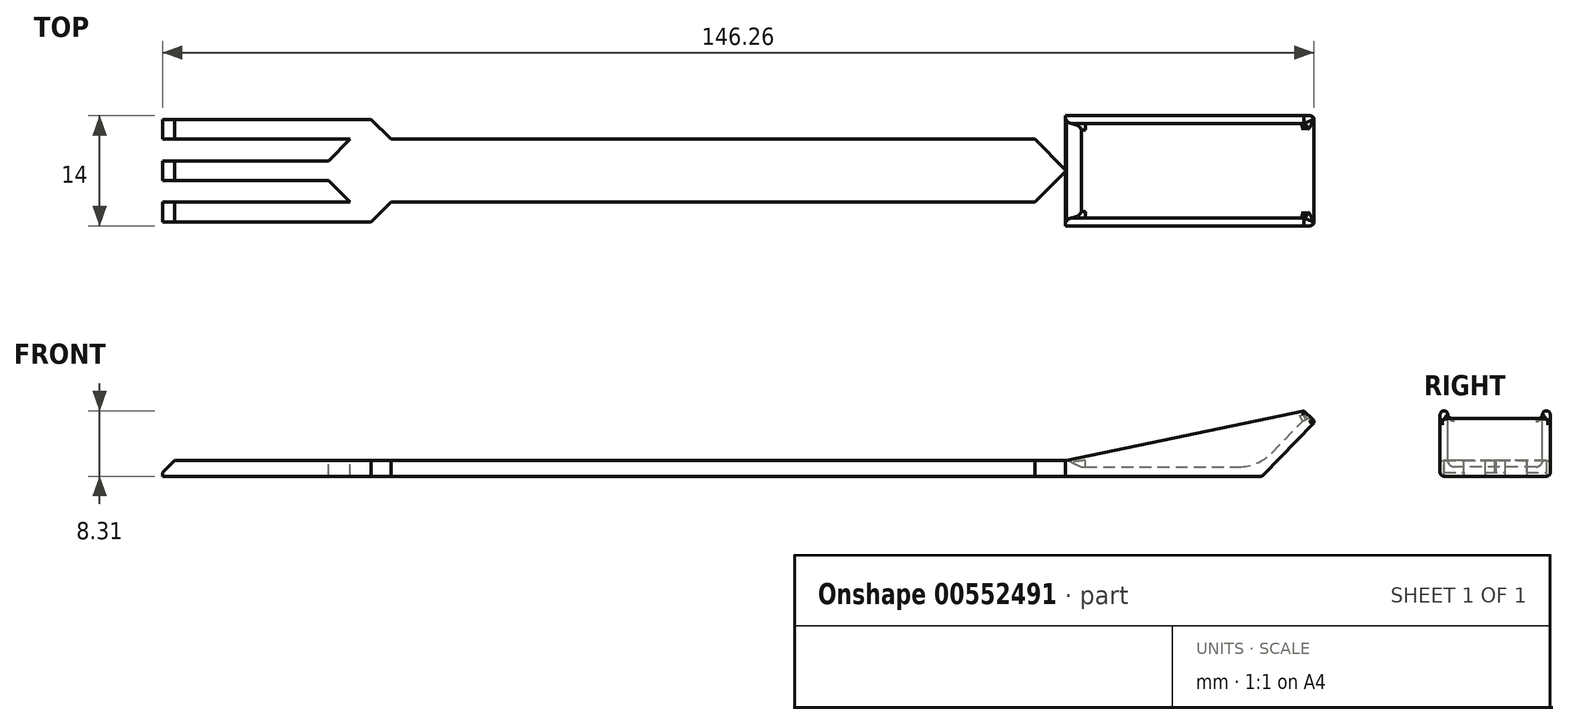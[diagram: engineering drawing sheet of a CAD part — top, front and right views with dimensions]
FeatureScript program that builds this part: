
annotation { "Feature Type Name" : "Feature", "Feature Type Description" : "" }
export const myFeature = defineFeature(function(context is Context, id is Id, definition is map)
    precondition{}
    {
        {
            var Q0;
            Q0=qCreatedBy(makeId("Top.planeOp"),FACE);
            var sketch = newSketch(context, id + "F0", { "sketchPlane" : qUnion([Q0])});
            skLineSegment(sketch, "E0.bottom", {"start": v(-44.04, 8) * mm, "end": v(45.74, 8) * mm});
            skLineSegment(sketch, "E0.top", {"start": v(-44.04, 0) * mm, "end": v(45.74, 0) * mm});
            skLineSegment(sketch, "E1.bottom", {"start": v(-44.5, 8) * mm, "end": v(-69.04, 8) * mm});
            skLineSegment(sketch, "E1.top", {"start": v(-44.04, 10.5) * mm, "end": v(-69.04, 10.5) * mm});
            skLineSegment(sketch, "E1.left", {"start": v(-44.04, 8) * mm, "end": v(-44.04, 10.5) * mm});
            skLineSegment(sketch, "E1.right", {"start": v(-69.04, 8) * mm, "end": v(-69.04, 10.5) * mm});
            skLineSegment(sketch, "E2.bottom", {"start": v(-44.5, 0) * mm, "end": v(-69.04, 0) * mm});
            skLineSegment(sketch, "E2.top", {"start": v(-44.04, -2.5) * mm, "end": v(-69.04, -2.5) * mm});
            skLineSegment(sketch, "E2.left", {"start": v(-44.04, 0) * mm, "end": v(-44.04, -2.5) * mm});
            skLineSegment(sketch, "E2.right", {"start": v(-69.04, 0) * mm, "end": v(-69.04, -2.5) * mm});
            skPoint(sketch, "E3.left.start.orphan", {"position": v(-44.04, 4) * mm});
            skPoint(sketch, "E3.right.end.orphan", {"position": v(-69.04, 2.75) * mm});
            skLineSegment(sketch, "E4.bottom", {"start": v(-69.04, 2.75) * mm, "end": v(-44.5, 2.75) * mm});
            skLineSegment(sketch, "E4.top", {"start": v(-69.04, 5.25) * mm, "end": v(-44.5, 5.25) * mm});
            skLineSegment(sketch, "E4.left", {"start": v(-69.04, 2.75) * mm, "end": v(-69.04, 5.25) * mm});
            skLineSegment(sketch, "E5.bottom", {"start": v(-44.04, 10.5) * mm, "end": v(-44.5, 10.5) * mm});
            skLineSegment(sketch, "E5.top", {"start": v(-44.04, -2.5) * mm, "end": v(-44.5, -2.5) * mm});
            skLineSegment(sketch, "E5.left", {"start": v(-44.04, 10.5) * mm, "end": v(-44.04, 8) * mm});
            skLineSegment(sketch, "E5.right", {"start": v(-44.5, 8) * mm, "end": v(-44.5, 5.25) * mm});
            skLineSegment(sketch, "E6.trimOffspring", {"start": v(-44.5, 2.75) * mm, "end": v(-44.5, 0) * mm});
            skLineSegment(sketch, "E7", {"start": v(45.74, 8) * mm, "end": v(45.74, 0) * mm});
            skSolve(sketch);
        }
        {
            var Q0;
            Q0 = qSketchRegion(id + "F0", true);
            extrude(context, id + "F1", {"entities" : qUnion([Q0]), "depth" : 2 * mm, "offsetDistance" : 25 * mm});
        }
        {
            var Q0;
            Q0=makeQuery(id+"F1.opExtrude","SWEPT_EDGE",EDGE,{"disambiguationData":[OSD([sQuery(id+"F0.wireOp",EDGE,"E0.top"),sQuery(id+"F0.wireOp",EDGE,"E2.left")])]});
            var Q1;
            Q1=makeQuery(id+"F1.opExtrude","SWEPT_EDGE",EDGE,{"disambiguationData":[OSD([sQuery(id+"F0.wireOp",EDGE,"E0.bottom"),sQuery(id+"F0.wireOp",EDGE,"E5.left")])]});
            chamfer(context, id + "F2", {"entities" : qUnion([Q0, Q1]), "width" : 4 * mm, "tangentPropagation" : true});
        }
        {
            var Q0;
            Q0=makeQuery(id+"F1.opExtrude","SWEPT_EDGE",EDGE,{"disambiguationData":[OSD([sQuery(id+"F0.wireOp",EDGE,"E4.bottom"),sQuery(id+"F0.wireOp",EDGE,"E6.trimOffspring")])]});
            var Q1;
            Q1=makeQuery(id+"F1.opExtrude","SWEPT_EDGE",EDGE,{"disambiguationData":[OSD([sQuery(id+"F0.wireOp",EDGE,"E4.top"),sQuery(id+"F0.wireOp",EDGE,"E5.right")])]});
            chamfer(context, id + "F3", {"entities" : qUnion([Q0, Q1]), "width" : 3.5 * mm, "tangentPropagation" : true});
        }
        {
            var Q0;
            Q0=qCreatedBy(makeId("Front.planeOp"),FACE);
            var sketch = newSketch(context, id + "F4", { "sketchPlane" : qUnion([Q0])});
            skLineSegment(sketch, "E8", {"start": v(45.64, 0) * mm, "end": v(70.64, 0) * mm});
            skLineSegment(sketch, "E9", {"start": v(70.64, 0) * mm, "end": v(77.36, 6.93) * mm});
            skLineSegment(sketch, "E10", {"start": v(77.36, 6.93) * mm, "end": v(75.93, 8.31) * mm});
            skLineSegment(sketch, "E11", {"start": v(75.93, 8.31) * mm, "end": v(45.64, 2) * mm});
            skLineSegment(sketch, "E12", {"start": v(45.64, 2) * mm, "end": v(45.64, 0) * mm});
            skSolve(sketch);
        }
        {
            var Q0;
            Q0=makeQuery(id+"F4.imprint","IMPRINT",FACE,{"disambiguationData":[TD([[makeQuery(id+"F4.imprint","IMPRINT",EDGE,{"derivedFrom":sQuery(id+"F4.wireOp",EDGE,"E8")}),1.0]])]});
            extrude(context, id + "F5", {"entities" : qUnion([Q0]), "operationType" : NewBodyOperationType.ADD, "oppositeDirection" : true, "depth" : 11 * mm, "offsetDistance" : 25 * mm});
        }
        {
            var Q0;
            Q0 = qSketchRegion(id + "F4", true);
            extrude(context, id + "F6", {"entities" : qUnion([Q0]), "operationType" : NewBodyOperationType.ADD, "depth" : 3 * mm, "offsetDistance" : 25 * mm});
        }
        {
            var Q0;
            Q0=qCreatedBy(makeId("Front.planeOp"),FACE);
            var sketch = newSketch(context, id + "F7", { "sketchPlane" : qUnion([Q0])});
            skLineSegment(sketch, "E13.0", {"start": v(40.64, 2) * mm, "end": v(40.64, 0) * mm});
            skLineSegment(sketch, "E14.2", {"start": v(70.13, 1.2) * mm, "end": v(75.66, 6.9) * mm});
            skLineSegment(sketch, "E14.3", {"start": v(47.64, 1.2) * mm, "end": v(70.13, 1.2) * mm});
            skLineSegment(sketch, "E15", {"start": v(47.64, 1.2) * mm, "end": v(45.28, 2.26) * mm});
            skLineSegment(sketch, "E16", {"start": v(45.28, 2.26) * mm, "end": v(75.32, 10.8) * mm});
            skLineSegment(sketch, "E17", {"start": v(75.32, 10.8) * mm, "end": v(80.5, 9.3) * mm});
            skLineSegment(sketch, "E18", {"start": v(80.5, 9.3) * mm, "end": v(75.66, 6.9) * mm});
            skSolve(sketch);
        }
        {
            var Q0;
            Q0=makeQuery(id+"F7.imprint","IMPRINT",FACE,{"disambiguationData":[TD([[makeQuery(id+"F7.imprint","IMPRINT",EDGE,{"derivedFrom":sQuery(id+"F7.wireOp",EDGE,"E14.2")}),1.0]])]});
            extrude(context, id + "F8", {"entities" : qUnion([Q0]), "operationType" : NewBodyOperationType.REMOVE, "oppositeDirection" : true, "depth" : 10 * mm, "offsetDistance" : 25 * mm});
        }
        {
            var Q0;
            Q0 = qSketchRegion(id + "F7", true);
            extrude(context, id + "F9", {"entities" : qUnion([Q0]), "operationType" : NewBodyOperationType.REMOVE, "oppositeDirection" : true, "depth" : -2 * mm, "offsetDistance" : 25 * mm});
        }
        {
            var Q0;
            {var subQ0=sQuery(id+"F7.wireOp",EDGE,"E14.3");var subQ1=sQuery(id+"F7.wireOp",EDGE,"E14.2");Q0=makeQuery(id+"F9.boolean.opBoolean","MERGE",EDGE,{"derivedFrom":[makeQuery(id+"F8.boolean.opBoolean","COPY",EDGE,{"derivedFrom":makeQuery(id+"F8.opExtrude","SWEPT_EDGE",EDGE,{"disambiguationData":[OSD([subQ1,subQ0])]})}),makeQuery(id+"F9.opExtrude","SWEPT_EDGE",EDGE,{"disambiguationData":[OSD([subQ1,subQ0])]})]});}
            fillet(context, id + "F10", {"entities" : qUnion([Q0]), "radius" : 5.82 * mm, "tangentPropagation" : true, "allowEdgeOverflow" : false});
        }
        {
            var Q0;
            {var subQ0=sQuery(id+"F4.wireOp",EDGE,"E9");var subQ1=sQuery(id+"F4.wireOp",EDGE,"E8");Q0=makeQuery(id+"F6.boolean.opBoolean","MERGE",EDGE,{"derivedFrom":[makeQuery(id+"F5.opExtrude","SWEPT_EDGE",EDGE,{"disambiguationData":[OSD([subQ1,subQ0])]}),makeQuery(id+"F6.opExtrude","SWEPT_EDGE",EDGE,{"disambiguationData":[OSD([subQ1,subQ0])]})]});}
            var Q1;
            Q1=makeQuery(id+"F6.opExtrude","CAP_EDGE",EDGE,{"disambiguationData":[OSD([sQuery(id+"F4.wireOp",EDGE,"E8")])],"isStart":false});
            var Q2;
            Q2=makeQuery(id+"F6.opExtrude","CAP_EDGE",EDGE,{"disambiguationData":[OSD([sQuery(id+"F4.wireOp",EDGE,"E9")])],"isStart":false});
            var Q3;
            Q3=makeQuery(id+"F5.opExtrude","CAP_EDGE",EDGE,{"disambiguationData":[OSD([sQuery(id+"F4.wireOp",EDGE,"E9")])],"isStart":false});
            var Q4;
            Q4=makeQuery(id+"F5.opExtrude","CAP_EDGE",EDGE,{"disambiguationData":[OSD([sQuery(id+"F4.wireOp",EDGE,"E8")])],"isStart":false});
            var Q5;
            {var subQ0=sQuery(id+"F7.wireOp",EDGE,"E18");var subQ1=sQuery(id+"F7.wireOp",EDGE,"E14.2");Q5=makeQuery(id+"F9.boolean.opBoolean","MERGE",EDGE,{"derivedFrom":[makeQuery(id+"F8.boolean.opBoolean","COPY",EDGE,{"derivedFrom":makeQuery(id+"F8.opExtrude","SWEPT_EDGE",EDGE,{"disambiguationData":[OSD([subQ1,subQ0])]})}),makeQuery(id+"F9.opExtrude","SWEPT_EDGE",EDGE,{"disambiguationData":[OSD([subQ1,subQ0])]})]});}
            var Q6;
            {var subQ0=sQuery(id+"F4.wireOp",EDGE,"E10");Q6=makeQuery(id+"F9.boolean.opBoolean","INTERSECT",EDGE,{"derivedFrom":[makeQuery(id+"F6.boolean.opBoolean","MERGE",FACE,{"derivedFrom":[makeQuery(id+"F5.opExtrude","SWEPT_FACE",FACE,{"disambiguationData":[OSD([subQ0])]}),makeQuery(id+"F6.opExtrude","SWEPT_FACE",FACE,{"disambiguationData":[OSD([subQ0])]})]}),makeQuery(id+"F9.opExtrude","SWEPT_FACE",FACE,{"disambiguationData":[OSD([sQuery(id+"F7.wireOp",EDGE,"E18")])]})]});}
            var Q7;
            {var subQ0=sQuery(id+"F4.wireOp",EDGE,"E10");Q7=makeQuery(id+"F8.boolean.opBoolean","INTERSECT",EDGE,{"derivedFrom":[makeQuery(id+"F6.boolean.opBoolean","MERGE",FACE,{"derivedFrom":[makeQuery(id+"F5.opExtrude","SWEPT_FACE",FACE,{"disambiguationData":[OSD([subQ0])]}),makeQuery(id+"F6.opExtrude","SWEPT_FACE",FACE,{"disambiguationData":[OSD([subQ0])]})]}),makeQuery(id+"F8.opExtrude","CAP_FACE",FACE,{"disambiguationData":[OSD([sQuery(id+"F7.wireOp",EDGE,"E14.2"),sQuery(id+"F7.wireOp",EDGE,"E14.3"),sQuery(id+"F7.wireOp",EDGE,"E15"),sQuery(id+"F7.wireOp",EDGE,"E16"),sQuery(id+"F7.wireOp",EDGE,"E17"),sQuery(id+"F7.wireOp",EDGE,"E18")])],"isStart":false})]});}
            var Q8;
            {var subQ0=sQuery(id+"F4.wireOp",EDGE,"E11");Q8=makeQuery(id+"F8.boolean.opBoolean","INTERSECT",EDGE,{"derivedFrom":[makeQuery(id+"F6.boolean.opBoolean","MERGE",FACE,{"derivedFrom":[makeQuery(id+"F5.opExtrude","SWEPT_FACE",FACE,{"disambiguationData":[OSD([subQ0])]}),makeQuery(id+"F6.opExtrude","SWEPT_FACE",FACE,{"disambiguationData":[OSD([subQ0])]})]}),makeQuery(id+"F8.opExtrude","CAP_FACE",FACE,{"disambiguationData":[OSD([sQuery(id+"F7.wireOp",EDGE,"E14.2"),sQuery(id+"F7.wireOp",EDGE,"E14.3"),sQuery(id+"F7.wireOp",EDGE,"E15"),sQuery(id+"F7.wireOp",EDGE,"E16"),sQuery(id+"F7.wireOp",EDGE,"E17"),sQuery(id+"F7.wireOp",EDGE,"E18")])],"isStart":false})]});}
            var Q9;
            {var subQ0=sQuery(id+"F4.wireOp",EDGE,"E11");Q9=makeQuery(id+"F9.boolean.opBoolean","INTERSECT",EDGE,{"derivedFrom":[makeQuery(id+"F6.boolean.opBoolean","MERGE",FACE,{"derivedFrom":[makeQuery(id+"F5.opExtrude","SWEPT_FACE",FACE,{"disambiguationData":[OSD([subQ0])]}),makeQuery(id+"F6.opExtrude","SWEPT_FACE",FACE,{"disambiguationData":[OSD([subQ0])]})]}),makeQuery(id+"F9.opExtrude","CAP_FACE",FACE,{"disambiguationData":[OSD([sQuery(id+"F7.wireOp",EDGE,"E14.2"),sQuery(id+"F7.wireOp",EDGE,"E14.3"),sQuery(id+"F7.wireOp",EDGE,"E15"),sQuery(id+"F7.wireOp",EDGE,"E16"),sQuery(id+"F7.wireOp",EDGE,"E17"),sQuery(id+"F7.wireOp",EDGE,"E18")])],"isStart":false})]});}
            var Q10;
            {var subQ0=sQuery(id+"F4.wireOp",EDGE,"E10");Q10=makeQuery(id+"F9.boolean.opBoolean","INTERSECT",EDGE,{"derivedFrom":[makeQuery(id+"F6.boolean.opBoolean","MERGE",FACE,{"derivedFrom":[makeQuery(id+"F5.opExtrude","SWEPT_FACE",FACE,{"disambiguationData":[OSD([subQ0])]}),makeQuery(id+"F6.opExtrude","SWEPT_FACE",FACE,{"disambiguationData":[OSD([subQ0])]})]}),makeQuery(id+"F9.opExtrude","CAP_FACE",FACE,{"disambiguationData":[OSD([sQuery(id+"F7.wireOp",EDGE,"E14.2"),sQuery(id+"F7.wireOp",EDGE,"E14.3"),sQuery(id+"F7.wireOp",EDGE,"E15"),sQuery(id+"F7.wireOp",EDGE,"E16"),sQuery(id+"F7.wireOp",EDGE,"E17"),sQuery(id+"F7.wireOp",EDGE,"E18")])],"isStart":false})]});}
            var Q11;
            Q11=makeQuery(id+"F6.opExtrude","CAP_EDGE",EDGE,{"disambiguationData":[OSD([sQuery(id+"F4.wireOp",EDGE,"E11")])],"isStart":false});
            var Q12;
            Q12=makeQuery(id+"F6.opExtrude","CAP_EDGE",EDGE,{"disambiguationData":[OSD([sQuery(id+"F4.wireOp",EDGE,"E10")])],"isStart":false});
            var Q13;
            Q13=makeQuery(id+"F5.opExtrude","CAP_EDGE",EDGE,{"disambiguationData":[OSD([sQuery(id+"F4.wireOp",EDGE,"E11")])],"isStart":false});
            var Q14;
            Q14=makeQuery(id+"F5.opExtrude","CAP_EDGE",EDGE,{"disambiguationData":[OSD([sQuery(id+"F4.wireOp",EDGE,"E10")])],"isStart":false});
            fillet(context, id + "F11", {"entities" : qUnion([Q0, Q1, Q2, Q3, Q4, Q5, Q6, Q7, Q8, Q9, Q10, Q11, Q12, Q13, Q14]), "radius" : .5 * mm, "tangentPropagation" : true, "allowEdgeOverflow" : false});
        }
        {
            var Q0;
            {var subQ0=sQuery(id+"F4.wireOp",EDGE,"E10");var subQ1=sQuery(id+"F4.wireOp",EDGE,"E9");Q0=makeQuery(id+"F6.boolean.opBoolean","MERGE",EDGE,{"derivedFrom":[makeQuery(id+"F5.opExtrude","SWEPT_EDGE",EDGE,{"disambiguationData":[OSD([subQ1,subQ0])]}),makeQuery(id+"F6.opExtrude","SWEPT_EDGE",EDGE,{"disambiguationData":[OSD([subQ1,subQ0])]})]});}
            fillet(context, id + "F12", {"entities" : qUnion([Q0]), "radius" : 0.34 * mm, "tangentPropagation" : true, "allowEdgeOverflow" : false});
        }
        {
            var Q0;
            {var subQ0=sQuery(id+"F7.wireOp",EDGE,"E14.3");var subQ1=sQuery(id+"F7.wireOp",EDGE,"E14.2");Q0=makeQuery(id+"F10.opFillet","BLEND_EDGE",EDGE,{"blendedFrom":[makeQuery(id+"F9.boolean.opBoolean","MERGE",EDGE,{"derivedFrom":[makeQuery(id+"F8.boolean.opBoolean","COPY",EDGE,{"derivedFrom":makeQuery(id+"F8.opExtrude","SWEPT_EDGE",EDGE,{"disambiguationData":[OSD([subQ1,subQ0])]})}),makeQuery(id+"F9.opExtrude","SWEPT_EDGE",EDGE,{"disambiguationData":[OSD([subQ1,subQ0])]})]}),makeQuery(id+"F8.boolean.opBoolean","COPY",FACE,{"derivedFrom":makeQuery(id+"F8.opExtrude","CAP_FACE",FACE,{"disambiguationData":[OSD([subQ1,subQ0,sQuery(id+"F7.wireOp",EDGE,"E15"),sQuery(id+"F7.wireOp",EDGE,"E16"),sQuery(id+"F7.wireOp",EDGE,"E17"),sQuery(id+"F7.wireOp",EDGE,"E18")])],"isStart":false})})],"blendedInto":[makeQuery(id+"F8.boolean.opBoolean","COPY",FACE,{"derivedFrom":makeQuery(id+"F8.opExtrude","CAP_FACE",FACE,{"disambiguationData":[OSD([subQ1,subQ0,sQuery(id+"F7.wireOp",EDGE,"E15"),sQuery(id+"F7.wireOp",EDGE,"E16"),sQuery(id+"F7.wireOp",EDGE,"E17"),sQuery(id+"F7.wireOp",EDGE,"E18")])],"isStart":false})})]});}
            var Q1;
            {var subQ0=sQuery(id+"F7.wireOp",EDGE,"E14.3");var subQ1=sQuery(id+"F7.wireOp",EDGE,"E14.2");Q1=makeQuery(id+"F10.opFillet","BLEND_EDGE",EDGE,{"blendedFrom":[makeQuery(id+"F9.boolean.opBoolean","MERGE",EDGE,{"derivedFrom":[makeQuery(id+"F8.boolean.opBoolean","COPY",EDGE,{"derivedFrom":makeQuery(id+"F8.opExtrude","SWEPT_EDGE",EDGE,{"disambiguationData":[OSD([subQ1,subQ0])]})}),makeQuery(id+"F9.opExtrude","SWEPT_EDGE",EDGE,{"disambiguationData":[OSD([subQ1,subQ0])]})]}),makeQuery(id+"F9.boolean.opBoolean","COPY",FACE,{"derivedFrom":makeQuery(id+"F9.opExtrude","CAP_FACE",FACE,{"disambiguationData":[OSD([subQ1,subQ0,sQuery(id+"F7.wireOp",EDGE,"E15"),sQuery(id+"F7.wireOp",EDGE,"E16"),sQuery(id+"F7.wireOp",EDGE,"E17"),sQuery(id+"F7.wireOp",EDGE,"E18")])],"isStart":false})})],"blendedInto":[makeQuery(id+"F9.boolean.opBoolean","COPY",FACE,{"derivedFrom":makeQuery(id+"F9.opExtrude","CAP_FACE",FACE,{"disambiguationData":[OSD([subQ1,subQ0,sQuery(id+"F7.wireOp",EDGE,"E15"),sQuery(id+"F7.wireOp",EDGE,"E16"),sQuery(id+"F7.wireOp",EDGE,"E17"),sQuery(id+"F7.wireOp",EDGE,"E18")])],"isStart":false})})]});}
            fillet(context, id + "F13", {"entities" : qUnion([Q0, Q1]), "radius" : 0.82 * mm, "tangentPropagation" : true, "allowEdgeOverflow" : false});
        }
        {
            var Q0;
            Q0=makeQuery(id+"F1.opExtrude","CAP_EDGE",EDGE,{"disambiguationData":[OSD([sQuery(id+"F0.wireOp",EDGE,"E4.left")])],"isStart":false});
            var Q1;
            Q1=makeQuery(id+"F1.opExtrude","CAP_EDGE",EDGE,{"disambiguationData":[OSD([sQuery(id+"F0.wireOp",EDGE,"E1.right")])],"isStart":false});
            var Q2;
            Q2=makeQuery(id+"F1.opExtrude","CAP_EDGE",EDGE,{"disambiguationData":[OSD([sQuery(id+"F0.wireOp",EDGE,"E2.right")])],"isStart":false});
            chamfer(context, id + "F14", {"entities" : qUnion([Q0, Q1, Q2]), "width" : 1.5 * mm, "tangentPropagation" : true});
        }
    });
